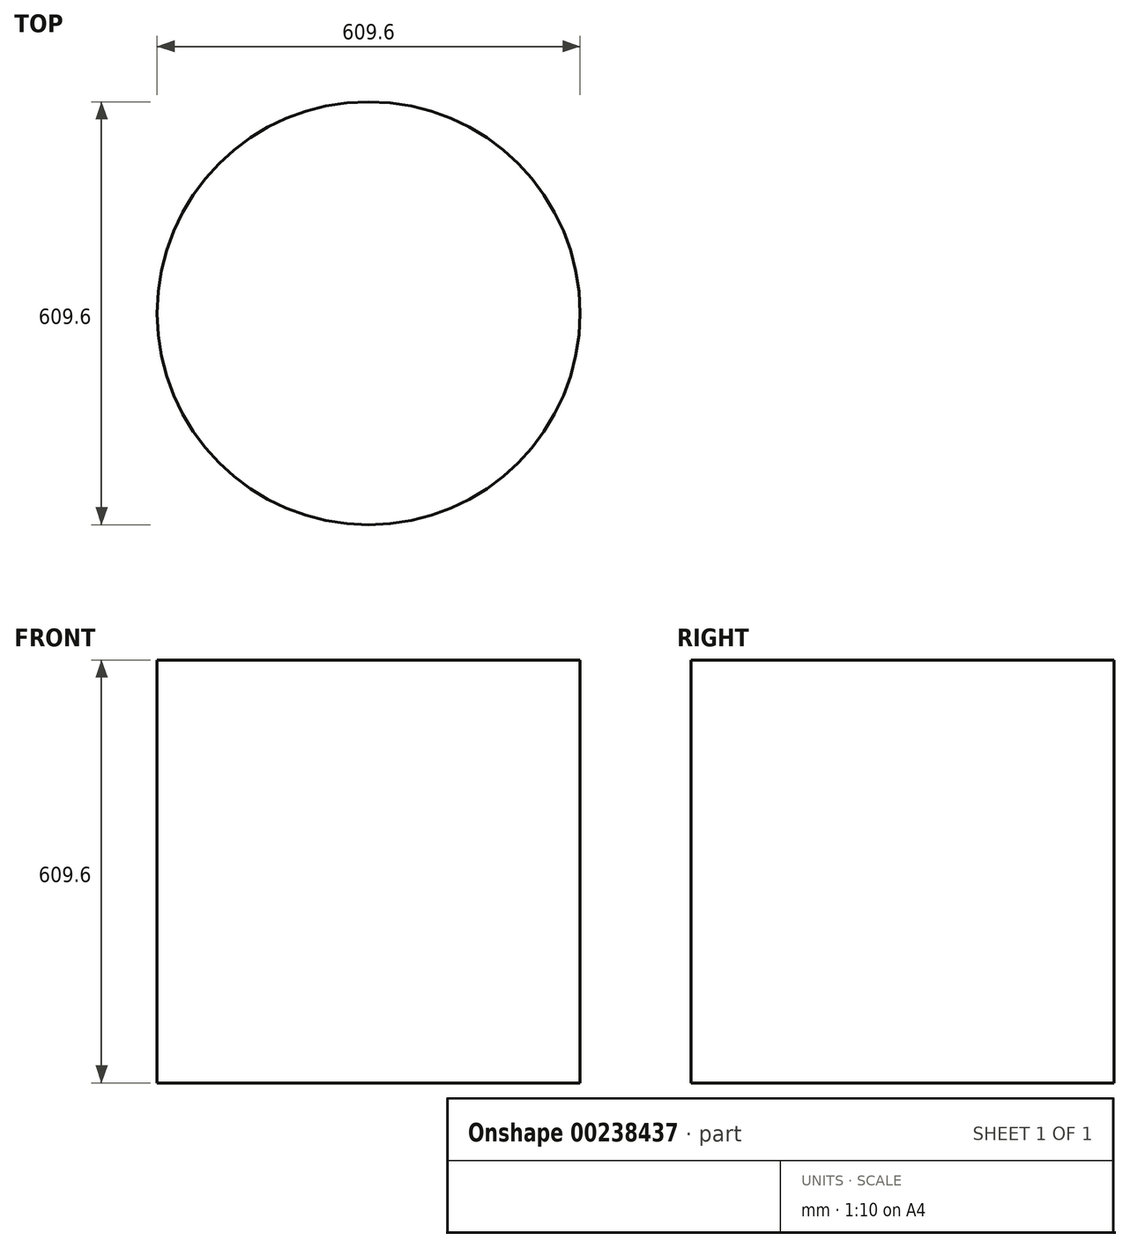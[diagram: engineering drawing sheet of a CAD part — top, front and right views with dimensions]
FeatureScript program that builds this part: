
annotation { "Feature Type Name" : "Feature", "Feature Type Description" : "" }
export const myFeature = defineFeature(function(context is Context, id is Id, definition is map)
    precondition{}
    {
        {
            var Q0;
            Q0=qCreatedBy(makeId("Top.planeOp"),FACE);
            var sketch = newSketch(context, id + "F0", { "sketchPlane" : qUnion([Q0])});
            skCircle(sketch, "E0", {"center": v(0, 0) * mm, "radius": 304.8 * mm});
            skSolve(sketch);
        }
        {
            var Q0;
            Q0 = qSketchRegion(id + "F0", true);
            extrude(context, id + "F1", {"entities" : qUnion([Q0]), "oppositeDirection" : true, "depth" : 609.6 * mm});
        }
    });
